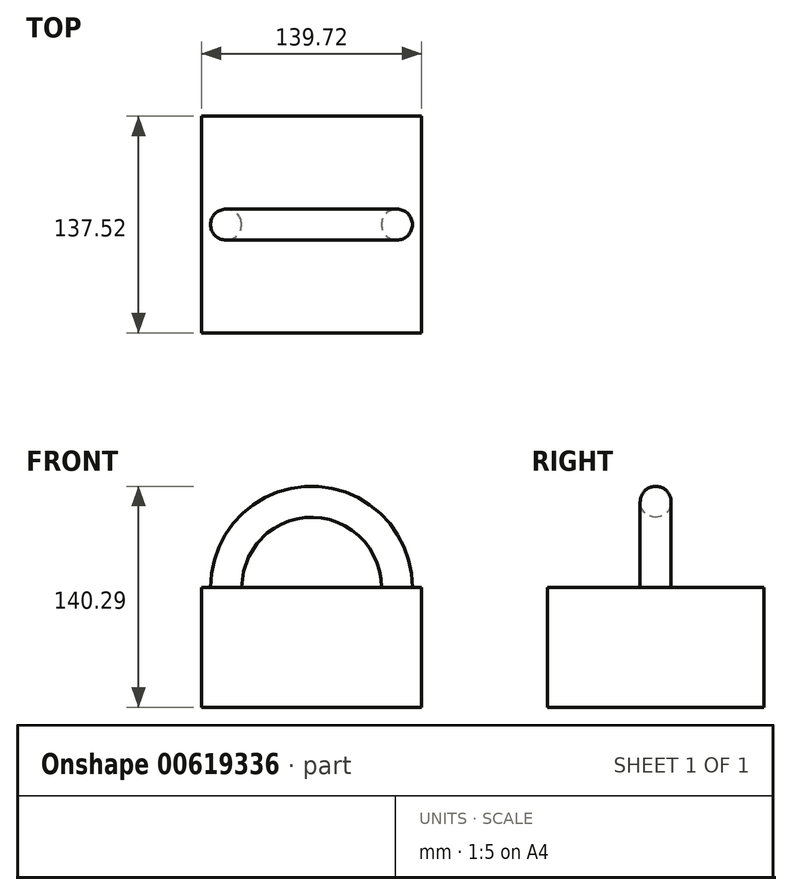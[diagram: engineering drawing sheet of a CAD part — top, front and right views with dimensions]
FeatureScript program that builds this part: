
annotation { "Feature Type Name" : "Feature", "Feature Type Description" : "" }
export const myFeature = defineFeature(function(context is Context, id is Id, definition is map)
    precondition{}
    {
        {
            var Q0;
            Q0=qCreatedBy(makeId("Top.planeOp"),FACE);
            var sketch = newSketch(context, id + "F0", { "sketchPlane" : qUnion([Q0])});
            skLineSegment(sketch, "E0.bottom", {"start": v(69.86, -68.76) * mm, "end": v(-69.86, -68.76) * mm});
            skLineSegment(sketch, "E0.top", {"start": v(69.86, 68.76) * mm, "end": v(-69.86, 68.76) * mm});
            skLineSegment(sketch, "E0.left", {"start": v(69.86, -68.76) * mm, "end": v(69.86, 68.76) * mm});
            skLineSegment(sketch, "E0.right", {"start": v(-69.86, -68.76) * mm, "end": v(-69.86, 68.76) * mm});
            skPoint(sketch, "E0.middle", {"position": v(0, 0) * mm});
            skLineSegment(sketch, "E1", {"start": v(0, 68.76) * mm, "end": v(0, -68.76) * mm});
            skSolve(sketch);
        }
        {
            var Q0;
            Q0=qCreatedBy(makeId("Top.planeOp"),FACE);
            var sketch = newSketch(context, id + "F1", { "sketchPlane" : qUnion([Q0])});
            skCircle(sketch, "E2", {"center": v(54.26, 0) * mm, "radius": 9.82 * mm});
            skSolve(sketch);
        }
        {
            var Q0;
            {var subQ0=sQuery(id+"F0.wireOp",EDGE,"E0.right");Q0=makeQuery(id+"F0.imprint","IMPRINT",FACE,{"disambiguationData":[TD([[makeQuery(id+"F0.imprint","IMPRINT",EDGE,{"derivedFrom":subQ0}),-1.0]])]});}
            var Q1;
            {var subQ0=sQuery(id+"F0.wireOp",EDGE,"E0.left");Q1=makeQuery(id+"F0.imprint","IMPRINT",FACE,{"disambiguationData":[TD([[makeQuery(id+"F0.imprint","IMPRINT",EDGE,{"derivedFrom":subQ0}),1.0]])]});}
            extrude(context, id + "F2", {"entities" : qUnion([Q0, Q1]), "oppositeDirection" : true, "depth" : 25.4 * mm, "offsetDistance" : 25.4 * mm});
        }
        {
            var Q0;
            Q0=makeQuery(id+"F2.opExtrude","CAP_FACE",FACE,{"disambiguationData":[OSD([sQuery(id+"F0.wireOp",EDGE,"E0.bottom"),sQuery(id+"F0.wireOp",EDGE,"E0.top"),sQuery(id+"F0.wireOp",EDGE,"E0.left"),sQuery(id+"F0.wireOp",EDGE,"E0.right")])],"isStart":false});
            extrude(context, id + "F3", {"entities" : qUnion([Q0]), "operationType" : NewBodyOperationType.ADD, "depth" : 25.4 * mm, "offsetDistance" : 25.4 * mm});
        }
        {
            var Q0;
            Q0=makeQuery(id+"F3.opExtrude","CAP_FACE",FACE,{"disambiguationData":[OSD([sQuery(id+"F0.wireOp",EDGE,"E0.bottom"),sQuery(id+"F0.wireOp",EDGE,"E0.top"),sQuery(id+"F0.wireOp",EDGE,"E0.left"),sQuery(id+"F0.wireOp",EDGE,"E0.right")])],"isStart":false});
            extrude(context, id + "F4", {"entities" : qUnion([Q0]), "operationType" : NewBodyOperationType.ADD, "depth" : 25.4 * mm, "offsetDistance" : 25.4 * mm});
        }
        {
            var Q0;
            Q0=makeQuery(id+"F1.imprint","IMPRINT",FACE,{"disambiguationData":[TD([[makeQuery(id+"F1.imprint","IMPRINT",EDGE,{"derivedFrom":sQuery(id+"F1.wireOp",EDGE,"E2")}),1.0]])]});
            var Q1;
            Q1=sQuery(id+"F0.wireOp",EDGE,"E1");
            revolve(context, id + "F5", {"operationType" : NewBodyOperationType.ADD, "entities" : qUnion([Q0]), "axis" : qUnion([Q1]), "revolveType" : RevolveType.FULL});
        }
    });
